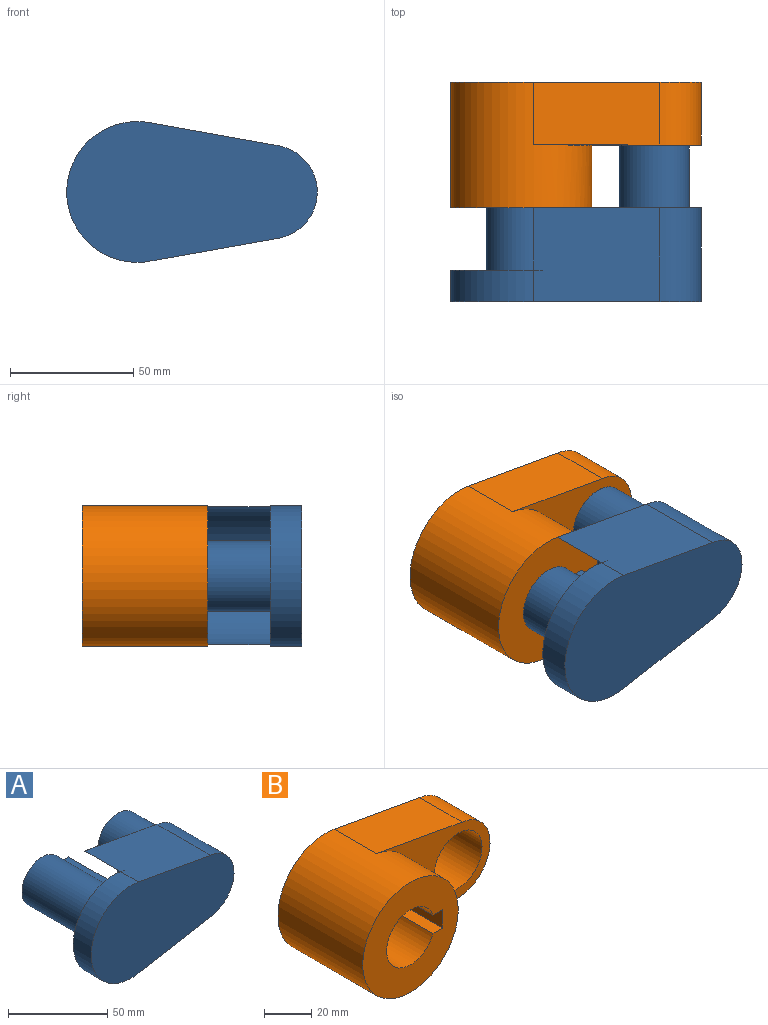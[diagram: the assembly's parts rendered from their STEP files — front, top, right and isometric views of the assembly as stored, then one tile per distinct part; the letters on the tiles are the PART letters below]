
ASSEMBLY  parts=2 mates=1
PART A: 15 faces, bbox 101.6x63.5x57.2 mm
  f0: cylinder r=14.29mm len=50.8mm, axis (0,-1,0), area 4067.1mm2, adj f1,f3,f4,f6
  f1: plane 50.8x5.58mm, normal (0,0,-1), area 283.4mm2, adj f0,f2,f4,f6
  f2: plane 50.8x9.53mm, normal (1,0,0), area 483.9mm2, adj f1,f3,f4,f6
  f3: plane 50.8x5.58mm, normal (0,0,1), area 283.4mm2, adj f0,f2,f4,f6
  f4: plane 33.34x28.58mm, normal (0,1,0), area 689.2mm2, adj f0,f1,f2,f3
  f5: cylinder r=28.57mm len=57.15mm, axis (0,-1,0), area 1286.8mm2, adj f6,f7,f9,f10
  f6: plane 57.15x57.15mm, normal (0,1,0), area 1876mm2, adj f0,f1,f2,f3,f5,f8
  f7: plane 101.6x57.15mm, normal (0,-1,0), area 4461.6mm2, adj f5,f9,f10,f11
  f8: cylinder r=28.57mm len=55.97mm, axis (0,-1,0), area 1986.7mm2, adj f6,f9,f10,f12
  f9: plane 51.23x38.1mm, normal (0.18,0,0.98), area 1983.1mm2, adj f5,f7,f8,f11,f12
  f10: plane 51.24x38.1mm, normal (0.18,0,-0.98), area 1983.1mm2, adj f5,f7,f8,f11,f12
  f11: cylinder r=19.05mm len=38.1mm, axis (0,-1,0), area 2051mm2, adj f7,f9,f10,f12
  f12: plane 67.97x55.97mm, normal (0,1,0), area 1255.1mm2, adj f8,f9,f10,f11,f13
  f13: cylinder r=14.29mm len=28.58mm, axis (0,-1,0), area 2280.2mm2, adj f12,f14
  f14: plane 28.58x28.58mm, normal (0,1,0), area 641.3mm2, adj f13
PART B: 12 faces, bbox 101.6x50.8x57.2 mm
  f0: plane 67.97x55.97mm, normal (0,-1,0), area 1255.1mm2, adj f1,f2,f3,f7,f9
  f1: cylinder r=28.57mm len=57.15mm, axis (0,1,0), area 7134mm2, adj f0,f2,f7,f10,f11
  f2: plane 51.24x25.4mm, normal (0.18,0,-0.98), area 1322mm2, adj f0,f1,f3,f10
  f3: cylinder r=19.05mm len=37.6mm, axis (0,1,0), area 1367.3mm2, adj f0,f2,f7,f10
  f4: cylinder r=14.29mm len=50.8mm, axis (0,1,0), area 4067.1mm2, adj f5,f8,f10,f11
  f5: plane 50.8x5.58mm, normal (0,0,-1), area 283.4mm2, adj f4,f6,f10,f11
  f6: plane 50.8x9.53mm, normal (-1,0,0), area 483.9mm2, adj f5,f8,f10,f11
  f7: plane 51.23x25.4mm, normal (0.18,0,0.98), area 1322mm2, adj f0,f1,f3,f10
  f8: plane 50.8x5.58mm, normal (0,0,1), area 283.4mm2, adj f4,f6,f10,f11
  f9: cylinder r=14.29mm len=28.58mm, axis (0,1,0), area 2280.2mm2, adj f0,f10
  f10: plane 101.6x57.15mm, normal (0,1,0), area 3131mm2, adj f1,f2,f3,f4,f5,f6,f7,f8
  f11: plane 57.15x57.15mm, normal (0,-1,0), area 1876mm2, adj f1,f4,f5,f6,f8
PLACE A t=(-20.49,-77.56,-9.21)mm
PLACE B t=(-36.01,11.29,-9.23)mm fixed
MATE slider B.f3 <-> A.f11  axis (0,1,0) through (17.97,-1.41,-9.23)mm
